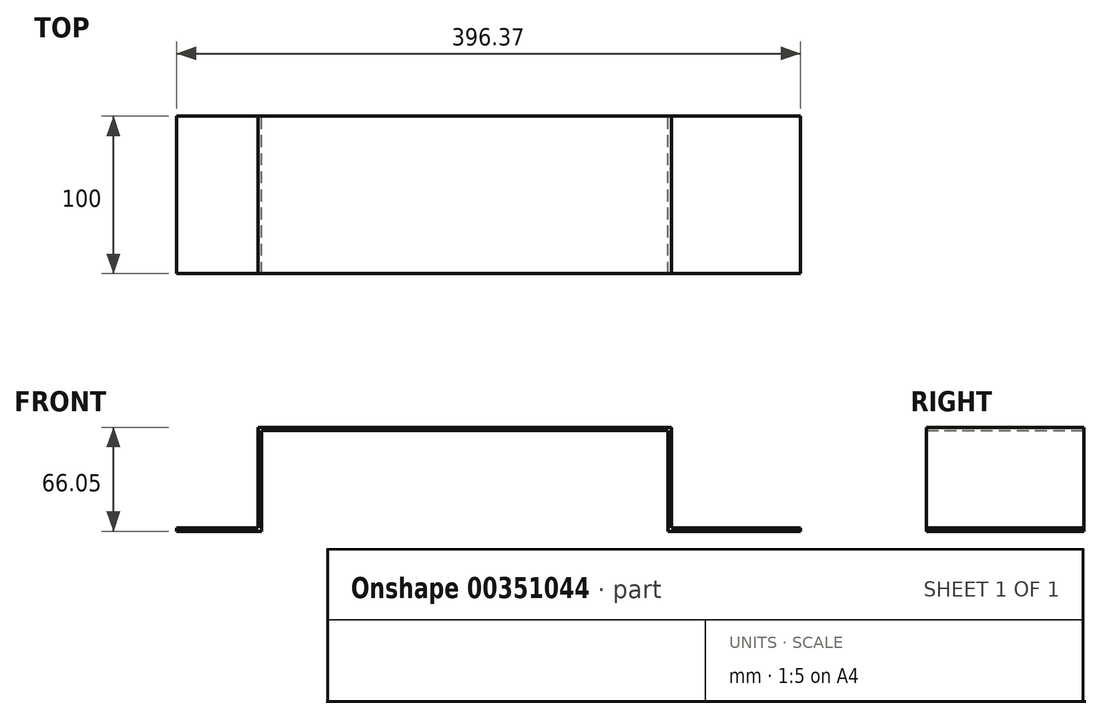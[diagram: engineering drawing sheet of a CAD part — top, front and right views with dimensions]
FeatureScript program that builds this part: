
annotation { "Feature Type Name" : "Feature", "Feature Type Description" : "" }
export const myFeature = defineFeature(function(context is Context, id is Id, definition is map)
    precondition{}
    {
        {
            var Q0;
            Q0=qCreatedBy(makeId("Front.planeOp"),FACE);
            var sketch = newSketch(context, id + "F0", { "sketchPlane" : qUnion([Q0])});
            skLineSegment(sketch, "E0.top", {"start": v(211.5, -66.05) * mm, "end": v(133.36, -66.05) * mm});
            skPoint(sketch, "E0.middle", {"position": v(0, 0) * mm});
            skLineSegment(sketch, "E1.bottom", {"start": v(211.5, -64.05) * mm, "end": v(129.5, -64.05) * mm});
            skLineSegment(sketch, "E2", {"start": v(-132.88, 0) * mm, "end": v(129.5, 0) * mm});
            skLineSegment(sketch, "E3", {"start": v(-184.88, -64.05) * mm, "end": v(-184.88, -66.05) * mm});
            skLineSegment(sketch, "E4", {"start": v(211.5, -64.05) * mm, "end": v(211.5, -66.05) * mm});
            skPoint(sketch, "E0.right.start.orphan", {"position": v(-221, 66.05) * mm});
            skPoint(sketch, "E5.orphan", {"position": v(-221, -66.05) * mm});
            skLineSegment(sketch, "E6", {"start": v(-132.88, 0) * mm, "end": v(-132.88, -64.05) * mm});
            skLineSegment(sketch, "E7", {"start": v(129.5, 0) * mm, "end": v(129.5, -64.05) * mm});
            skLineSegment(sketch, "E8.trimOffspring", {"start": v(-132.88, -64.05) * mm, "end": v(-184.88, -64.05) * mm});
            skLineSegment(sketch, "E9.trimOffspring", {"start": v(-133.36, -66.05) * mm, "end": v(-184.88, -66.05) * mm});
            skLineSegment(sketch, "E10.top", {"start": v(-130.88, -2) * mm, "end": v(127.5, -2) * mm});
            skLineSegment(sketch, "E10.left", {"start": v(-130.88, -66.05) * mm, "end": v(-130.88, -2) * mm});
            skLineSegment(sketch, "E10.right", {"start": v(127.5, -66.05) * mm, "end": v(127.5, -2) * mm});
            skLineSegment(sketch, "E11", {"start": v(-133.36, -66.05) * mm, "end": v(-130.88, -66.05) * mm});
            skLineSegment(sketch, "E12", {"start": v(127.5, -66.05) * mm, "end": v(133.36, -66.05) * mm});
            skSolve(sketch);
        }
        {
            var Q0;
            Q0=qSketchRegion(id+"F0",true);
            extrude(context, id + "F1", {"entities" : qUnion([Q0]), "depth" : 100 * mm});
        }
    });
